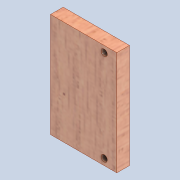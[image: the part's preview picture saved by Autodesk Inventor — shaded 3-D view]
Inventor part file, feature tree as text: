
AUTODESK INVENTOR PART (.ipt)
format: ipt  version: 2020 (Build 240168000, 168)  size: 161,792 bytes
history: native  units: mm
features: sketch x2, extrude x1, hole x1
ambient origin geometry x8: Origin, YZ Plane, XZ Plane, XY Plane, X Axis, Y Axis, Z Axis, Center Point
bodies: Solid1 (feature_tree)
feature tree (4):
  extrude  "Extrusion1"  Depth=66.0mm
  hole  "Hole1"  [1 undecoded]
  sketch  "Sketch1"  dims[d0=42.0mm d1=66.0mm]
  sketch  "Sketch4"  dims[d2=8.0mm d3=0.0mm d19=4.0mm d20=4.0mm d21=8.0mm d22=4.0mm d23=6.0mm d24=4.0mm d25=2.0mm d26=90.0deg d27=8.0mm d28=20.594885mm]
note: 1 required parameter value undecoded (feature->parameter linkage not recoverable at this tier; creation-order binding heuristic only, values carry confidence <= 0.55)
